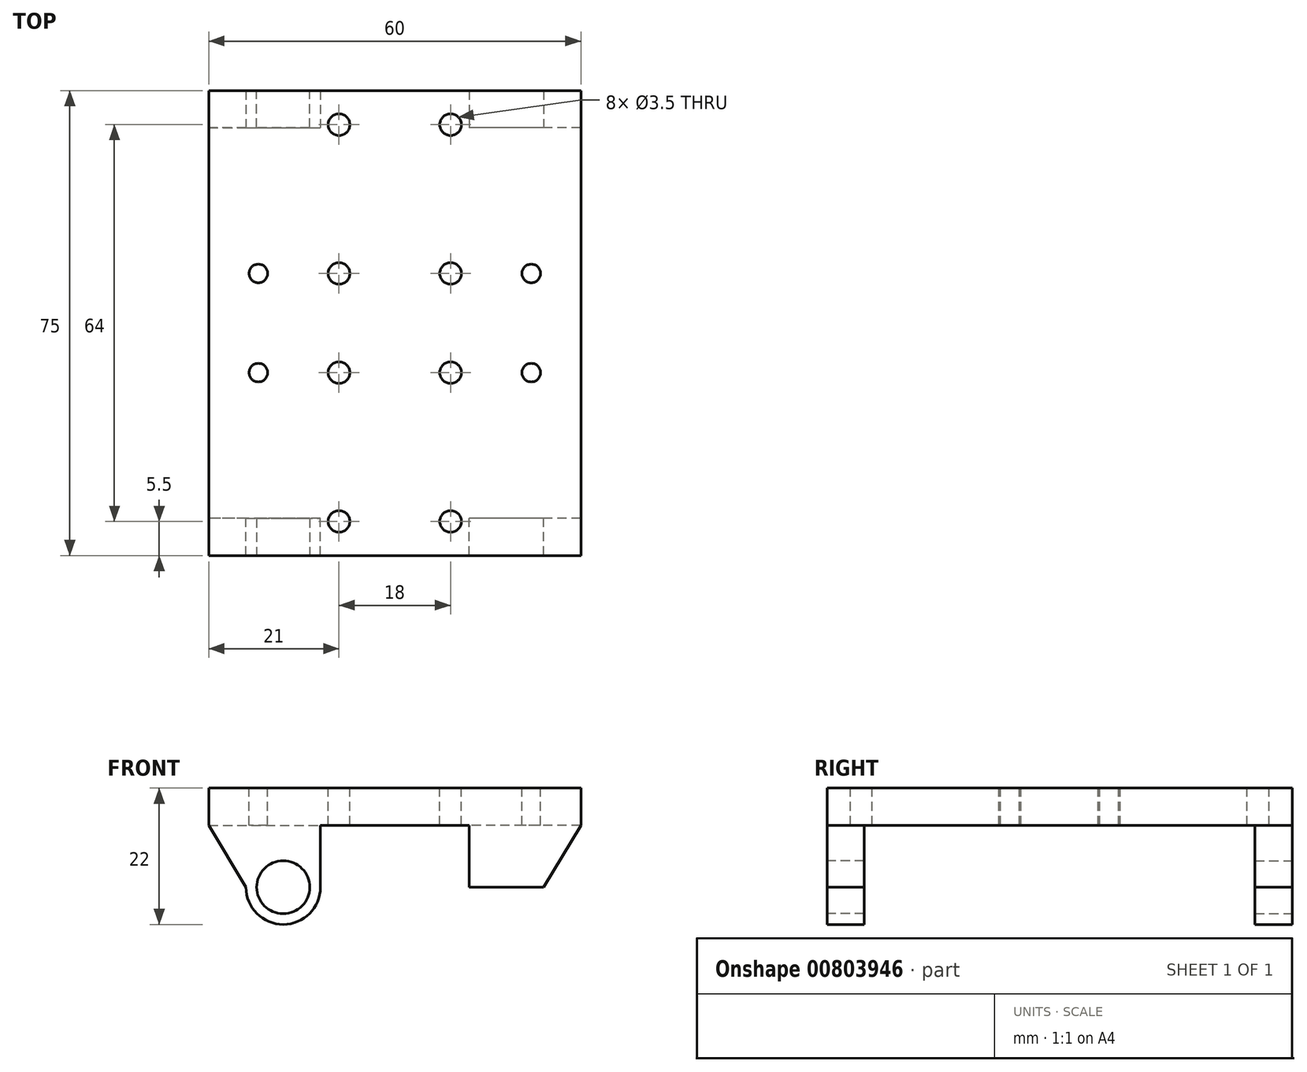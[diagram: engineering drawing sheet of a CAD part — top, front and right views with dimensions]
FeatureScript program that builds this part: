
annotation { "Feature Type Name" : "Feature", "Feature Type Description" : "" }
export const myFeature = defineFeature(function(context is Context, id is Id, definition is map)
    precondition{}
    {
        {
            var Q0;
            Q0=qCreatedBy(makeId("Top.planeOp"),FACE);
            var sketch = newSketch(context, id + "F0", { "sketchPlane" : qUnion([Q0])});
            skLineSegment(sketch, "E0.bottom", {"start": v(30, 37.5) * mm, "end": v(-30, 37.5) * mm});
            skLineSegment(sketch, "E0.top", {"start": v(30, -37.5) * mm, "end": v(-30, -37.5) * mm});
            skLineSegment(sketch, "E0.left", {"start": v(30, 37.5) * mm, "end": v(30, -37.5) * mm});
            skLineSegment(sketch, "E0.right", {"start": v(-30, 37.5) * mm, "end": v(-30, -37.5) * mm});
            skPoint(sketch, "E0.middle", {"position": v(0, 0) * mm});
            skLineSegment(sketch, "E1.bottom", {"start": v(-9, 32) * mm, "end": v(9, 32) * mm});
            skLineSegment(sketch, "E1.top", {"start": v(-9, 8) * mm, "end": v(9, 8) * mm});
            skLineSegment(sketch, "E1.left", {"start": v(-9, 32) * mm, "end": v(-9, 8) * mm});
            skLineSegment(sketch, "E1.right", {"start": v(9, 32) * mm, "end": v(9, 8) * mm});
            skPoint(sketch, "E1.middle", {"position": v(0, 20) * mm});
            skLineSegment(sketch, "E2.bottom", {"start": v(-9, -8) * mm, "end": v(9, -8) * mm});
            skLineSegment(sketch, "E2.top", {"start": v(-9, -32) * mm, "end": v(9, -32) * mm});
            skLineSegment(sketch, "E2.left", {"start": v(-9, -8) * mm, "end": v(-9, -32) * mm});
            skLineSegment(sketch, "E2.right", {"start": v(9, -8) * mm, "end": v(9, -32) * mm});
            skPoint(sketch, "E2.middle", {"position": v(0, -20) * mm});
            skLineSegment(sketch, "E3.bottom", {"start": v(24, 37.5) * mm, "end": v(12, 37.5) * mm});
            skLineSegment(sketch, "E3.top", {"start": v(24, 31.5) * mm, "end": v(12, 31.5) * mm});
            skLineSegment(sketch, "E3.left", {"start": v(24, 37.5) * mm, "end": v(24, 31.5) * mm});
            skLineSegment(sketch, "E3.right", {"start": v(12, 37.5) * mm, "end": v(12, 31.5) * mm});
            skLineSegment(sketch, "E4.bottom", {"start": v(-24, 37.5) * mm, "end": v(-12, 37.5) * mm});
            skLineSegment(sketch, "E4.top", {"start": v(-24, 31.5) * mm, "end": v(-12, 31.5) * mm});
            skLineSegment(sketch, "E4.left", {"start": v(-24, 37.5) * mm, "end": v(-24, 31.5) * mm});
            skLineSegment(sketch, "E4.right", {"start": v(-12, 37.5) * mm, "end": v(-12, 31.5) * mm});
            skLineSegment(sketch, "E5.bottom", {"start": v(24, -37.5) * mm, "end": v(12, -37.5) * mm});
            skLineSegment(sketch, "E5.top", {"start": v(24, -31.5) * mm, "end": v(12, -31.5) * mm});
            skLineSegment(sketch, "E5.left", {"start": v(24, -37.5) * mm, "end": v(24, -31.5) * mm});
            skLineSegment(sketch, "E5.right", {"start": v(12, -37.5) * mm, "end": v(12, -31.5) * mm});
            skLineSegment(sketch, "E6.bottom", {"start": v(-12, -37.5) * mm, "end": v(-24, -37.5) * mm});
            skLineSegment(sketch, "E6.top", {"start": v(-12, -31.5) * mm, "end": v(-24, -31.5) * mm});
            skLineSegment(sketch, "E6.left", {"start": v(-12, -37.5) * mm, "end": v(-12, -31.5) * mm});
            skLineSegment(sketch, "E6.right", {"start": v(-24, -37.5) * mm, "end": v(-24, -31.5) * mm});
            skPoint(sketch, "E7", {"position": v(22, 8) * mm});
            skPoint(sketch, "E8", {"position": v(22, -8) * mm});
            skPoint(sketch, "E9", {"position": v(-22, 8) * mm});
            skPoint(sketch, "E10", {"position": v(-22, -8) * mm});
            skSolve(sketch);
        }
        {
            var Q0;
            {var subQ5=sQuery(id+"F0.wireOp",EDGE,"E0.left");Q0=makeQuery(id+"F0.imprint","IMPRINT",FACE,{"disambiguationData":[TD([[makeQuery(id+"F0.imprint","IMPRINT",EDGE,{"derivedFrom":subQ5}),-1.0]])]});}
            var Q1;
            Q1=makeQuery(id+"F0.imprint","IMPRINT",FACE,{"disambiguationData":[TD([[makeQuery(id+"F0.imprint","IMPRINT",EDGE,{"derivedFrom":sQuery(id+"F0.wireOp",EDGE,"E1.bottom")}),-1.0]])]});
            var Q2;
            Q2=makeQuery(id+"F0.imprint","IMPRINT",FACE,{"disambiguationData":[TD([[makeQuery(id+"F0.imprint","IMPRINT",EDGE,{"derivedFrom":sQuery(id+"F0.wireOp",EDGE,"E2.bottom")}),-1.0]])]});
            var Q3;
            Q3=makeQuery(id+"F0.imprint","IMPRINT",FACE,{"disambiguationData":[TD([[makeQuery(id+"F0.imprint","IMPRINT",EDGE,{"derivedFrom":sQuery(id+"F0.wireOp",EDGE,"E5.top")}),1.0]])]});
            var Q4;
            Q4=makeQuery(id+"F0.imprint","IMPRINT",FACE,{"disambiguationData":[TD([[makeQuery(id+"F0.imprint","IMPRINT",EDGE,{"derivedFrom":sQuery(id+"F0.wireOp",EDGE,"E2.bottom")}),-1.0]])]});
            var Q5;
            {var subQ5=sQuery(id+"F0.wireOp",EDGE,"E0.left");Q5=makeQuery(id+"F0.imprint","IMPRINT",FACE,{"disambiguationData":[TD([[makeQuery(id+"F0.imprint","IMPRINT",EDGE,{"derivedFrom":subQ5}),-1.0]])]});}
            var Q6;
            Q6=makeQuery(id+"F0.imprint","IMPRINT",FACE,{"disambiguationData":[TD([[makeQuery(id+"F0.imprint","IMPRINT",EDGE,{"derivedFrom":sQuery(id+"F0.wireOp",EDGE,"E2.bottom")}),-1.0]])]});
            var Q7;
            Q7=makeQuery(id+"F0.imprint","IMPRINT",FACE,{"disambiguationData":[TD([[makeQuery(id+"F0.imprint","IMPRINT",EDGE,{"derivedFrom":sQuery(id+"F0.wireOp",EDGE,"E6.top")}),1.0]])]});
            var Q8;
            Q8=makeQuery(id+"F0.imprint","IMPRINT",FACE,{"disambiguationData":[TD([[makeQuery(id+"F0.imprint","IMPRINT",EDGE,{"derivedFrom":sQuery(id+"F0.wireOp",EDGE,"E1.bottom")}),-1.0]])]});
            var Q9;
            {var subQ5=sQuery(id+"F0.wireOp",EDGE,"E0.left");Q9=makeQuery(id+"F0.imprint","IMPRINT",FACE,{"disambiguationData":[TD([[makeQuery(id+"F0.imprint","IMPRINT",EDGE,{"derivedFrom":subQ5}),-1.0]])]});}
            var Q10;
            Q10=makeQuery(id+"F0.imprint","IMPRINT",FACE,{"disambiguationData":[TD([[makeQuery(id+"F0.imprint","IMPRINT",EDGE,{"derivedFrom":sQuery(id+"F0.wireOp",EDGE,"E4.top")}),1.0]])]});
            var Q11;
            Q11=makeQuery(id+"F0.imprint","IMPRINT",FACE,{"disambiguationData":[TD([[makeQuery(id+"F0.imprint","IMPRINT",EDGE,{"derivedFrom":sQuery(id+"F0.wireOp",EDGE,"E3.top")}),-1.0]])]});
            extrude(context, id + "F1", {"entities" : qUnion([Q0, Q1, Q2, Q3, Q4, Q5, Q6, Q7, Q8, Q9, Q10, Q11]), "depth" : 6 * mm, "offsetDistance" : 25 * mm});
        }
        {
            var Q0;
            Q0=sQuery(id+"F0.wireOp",VERTEX,"E1.bottom.end");
            var Q1;
            Q1=sQuery(id+"F0.wireOp",VERTEX,"E1.bottom.start");
            var Q2;
            Q2=sQuery(id+"F0.wireOp",VERTEX,"E1.top.start");
            var Q3;
            Q3=sQuery(id+"F0.wireOp",VERTEX,"E1.top.end");
            var Q4;
            Q4=sQuery(id+"F0.wireOp",VERTEX,"E2.bottom.end");
            var Q5;
            Q5=sQuery(id+"F0.wireOp",VERTEX,"E2.bottom.start");
            var Q6;
            Q6=sQuery(id+"F0.wireOp",VERTEX,"E2.top.start");
            var Q7;
            Q7=sQuery(id+"F0.wireOp",VERTEX,"E2.top.end");
            var Q8;
            Q8=makeQuery(id+"F1.opExtrude","SWEPT_BODY",BODY,{"disambiguationData":[OSD([sQuery(id+"F0.wireOp",EDGE,"E0.bottom"),sQuery(id+"F0.wireOp",EDGE,"E0.top"),sQuery(id+"F0.wireOp",EDGE,"E0.left"),sQuery(id+"F0.wireOp",EDGE,"E0.right")])]});
            hole(context, id + "F2", {"style" : HoleStyle.SIMPLE, "endStyle" : HoleEndStyle.THROUGH, "oppositeDirection" : true, "holeDiameter" : 3.5 * mm, "majorDiameter" : 5 * mm, "isTappedThrough" : true, "tappedDepth" : 12 * mm, "tapClearance" : 3, "locations" : qUnion([Q0, Q1, Q2, Q3, Q4, Q5, Q6, Q7]), "scope" : qUnion([Q8])});
        }
        {
            var Q0;
            Q0=makeQuery(id+"F0.imprint","IMPRINT",FACE,{"disambiguationData":[TD([[makeQuery(id+"F0.imprint","IMPRINT",EDGE,{"derivedFrom":sQuery(id+"F0.wireOp",EDGE,"E3.top")}),-1.0]])]});
            var Q1;
            Q1=makeQuery(id+"F0.imprint","IMPRINT",FACE,{"disambiguationData":[TD([[makeQuery(id+"F0.imprint","IMPRINT",EDGE,{"derivedFrom":sQuery(id+"F0.wireOp",EDGE,"E4.top")}),1.0]])]});
            var Q2;
            Q2=makeQuery(id+"F0.imprint","IMPRINT",FACE,{"disambiguationData":[TD([[makeQuery(id+"F0.imprint","IMPRINT",EDGE,{"derivedFrom":sQuery(id+"F0.wireOp",EDGE,"E6.top")}),1.0]])]});
            var Q3;
            Q3=makeQuery(id+"F0.imprint","IMPRINT",FACE,{"disambiguationData":[TD([[makeQuery(id+"F0.imprint","IMPRINT",EDGE,{"derivedFrom":sQuery(id+"F0.wireOp",EDGE,"E5.top")}),1.0]])]});
            extrude(context, id + "F3", {"entities" : qUnion([Q0, Q1, Q2, Q3]), "operationType" : NewBodyOperationType.ADD, "oppositeDirection" : true, "depth" : 10 * mm, "offsetDistance" : 25 * mm});
        }
        {
            var Q0;
            {var subQ0=sQuery(id+"F0.wireOp",EDGE,"E0.top");Q0=makeQuery(id+"F3.boolean.opBoolean","MERGE",FACE,{"derivedFrom":[makeQuery(id+"F1.opExtrude","SWEPT_FACE",FACE,{"disambiguationData":[OSD([subQ0])]}),makeQuery(id+"F3.opExtrude","SWEPT_FACE",FACE,{"disambiguationData":[OSD([subQ0]),TDD([makeQuery(id+"F0.imprint","IMPRINT",EDGE,{"disambiguationData":[TD([[makeQuery(id+"F0.imprint","INTERSECT",VERTEX,{"derivedFrom":[subQ0,sQuery(id+"F0.wireOp",EDGE,"E5.right")]}),1.0]])],"derivedFrom":subQ0})])]}),makeQuery(id+"F3.opExtrude","SWEPT_FACE",FACE,{"disambiguationData":[OSD([subQ0]),TDD([makeQuery(id+"F0.imprint","IMPRINT",EDGE,{"disambiguationData":[TD([[makeQuery(id+"F0.imprint","INTERSECT",VERTEX,{"derivedFrom":[subQ0,sQuery(id+"F0.wireOp",EDGE,"E6.left")]}),-1.0]])],"derivedFrom":subQ0})])]})]});}
            var sketch = newSketch(context, id + "F4", { "sketchPlane" : qUnion([Q0])});
            skLineSegment(sketch, "E11", {"start": v(30, 0) * mm, "end": v(24, -10) * mm});
            skArc(sketch, "E12", {"start": v(24, -10) * mm, "mid": v(18, -16) * mm, "end": v(12, -10) * mm});
            skLineSegment(sketch, "E13", {"start": v(-24, -10) * mm, "end": v(-30, 0) * mm});
            skArc(sketch, "E14", {"start": v(-24, -10) * mm, "mid": v(-18, -16) * mm, "end": v(-12, -10) * mm});
            skCircle(sketch, "E15", {"center": v(18, -10) * mm, "radius": 4.28 * mm});
            skCircle(sketch, "E16", {"center": v(-18, -10) * mm, "radius": 4.28 * mm});
            skSolve(sketch);
        }
        {
            var Q0;
            {var subQ0=sQuery(id+"F4.wireOp",EDGE,"E12");Q0=makeQuery(id+"F4.imprint","IMPRINT",FACE,{"disambiguationData":[TD([[makeQuery(id+"F4.imprint","IMPRINT",EDGE,{"derivedFrom":subQ0}),-1.0]])]});}
            var Q1;
            Q1=makeQuery(id+"F4.imprint","IMPRINT",FACE,{"disambiguationData":[TD([[makeQuery(id+"F4.imprint","IMPRINT",EDGE,{"derivedFrom":sQuery(id+"F4.wireOp",EDGE,"E11")}),-1.0]])]});
            var Q2;
            {var subQ0=sQuery(id+"F4.wireOp",EDGE,"E14");Q2=makeQuery(id+"F4.imprint","IMPRINT",FACE,{"disambiguationData":[TD([[makeQuery(id+"F4.imprint","IMPRINT",EDGE,{"derivedFrom":subQ0}),1.0]])]});}
            var Q3;
            Q3=makeQuery(id+"F4.imprint","IMPRINT",FACE,{"disambiguationData":[TD([[makeQuery(id+"F4.imprint","IMPRINT",EDGE,{"derivedFrom":sQuery(id+"F4.wireOp",EDGE,"E13")}),-1.0]])]});
            extrude(context, id + "F5", {"entities" : qUnion([Q0, Q1, Q2, Q3]), "operationType" : NewBodyOperationType.ADD, "oppositeDirection" : true, "depth" : 6 * mm, "offsetDistance" : 25 * mm});
        }
        {
            var Q0;
            {var subQ0=sQuery(id+"F4.wireOp",EDGE,"E15");var subQ1=sQuery(id+"F0.wireOp",EDGE,"E0.top");var subQ2=makeQuery(id+"F3.opExtrude","CAP_EDGE",EDGE,{"disambiguationData":[OSD([subQ1]),TDD([makeQuery(id+"F0.imprint","IMPRINT",EDGE,{"disambiguationData":[TD([[makeQuery(id+"F0.imprint","INTERSECT",VERTEX,{"derivedFrom":[subQ1,sQuery(id+"F0.wireOp",EDGE,"E5.right")]}),1.0]])],"derivedFrom":subQ1})])],"isStart":false});var subQ3=makeQuery(id+"F4.imprint","INTERSECT",VERTEX,{"disambiguationData":[OD(0.0)],"derivedFrom":[subQ2,subQ0]});Q0=makeQuery(id+"F4.imprint","IMPRINT",FACE,{"disambiguationData":[TD([[makeQuery(id+"F4.imprint","IMPRINT",EDGE,{"disambiguationData":[TD([[subQ3,1.0]])],"derivedFrom":subQ0}),1.0]])]});}
            var Q1;
            {var subQ0=sQuery(id+"F4.wireOp",EDGE,"E16");var subQ1=sQuery(id+"F0.wireOp",EDGE,"E0.top");var subQ2=makeQuery(id+"F3.opExtrude","CAP_EDGE",EDGE,{"disambiguationData":[OSD([subQ1]),TDD([makeQuery(id+"F0.imprint","IMPRINT",EDGE,{"disambiguationData":[TD([[makeQuery(id+"F0.imprint","INTERSECT",VERTEX,{"derivedFrom":[subQ1,sQuery(id+"F0.wireOp",EDGE,"E6.left")]}),-1.0]])],"derivedFrom":subQ1})])],"isStart":false});var subQ3=makeQuery(id+"F4.imprint","INTERSECT",VERTEX,{"disambiguationData":[OD(0.0)],"derivedFrom":[subQ2,subQ0]});Q1=makeQuery(id+"F4.imprint","IMPRINT",FACE,{"disambiguationData":[TD([[makeQuery(id+"F4.imprint","IMPRINT",EDGE,{"disambiguationData":[TD([[subQ3,-1.0]])],"derivedFrom":subQ0}),1.0]])]});}
            extrude(context, id + "F6", {"entities" : qUnion([Q0, Q1]), "operationType" : NewBodyOperationType.REMOVE, "oppositeDirection" : true, "depth" : 25 * mm, "offsetDistance" : 25 * mm});
        }
        {
            var Q0;
            Q0=makeQuery(id+"F1.opExtrude","SWEPT_BODY",BODY,{"disambiguationData":[OSD([sQuery(id+"F0.wireOp",EDGE,"E0.bottom"),sQuery(id+"F0.wireOp",EDGE,"E0.top"),sQuery(id+"F0.wireOp",EDGE,"E0.left"),sQuery(id+"F0.wireOp",EDGE,"E0.right")])]});
            var Q1;
            Q1=qCreatedBy(makeId("Front.planeOp"),FACE);
            mirror(context, id + "F7", {"operationType" : NewBodyOperationType.ADD, "entities" : qUnion([Q0]), "mirrorPlane" : qUnion([Q1])});
        }
        {
            var Q0;
            {var subQ0=sQuery(id+"F4.wireOp",EDGE,"E15");var subQ1=sQuery(id+"F0.wireOp",EDGE,"E0.top");var subQ2=makeQuery(id+"F3.opExtrude","CAP_EDGE",EDGE,{"disambiguationData":[OSD([subQ1]),TDD([makeQuery(id+"F0.imprint","IMPRINT",EDGE,{"disambiguationData":[TD([[makeQuery(id+"F0.imprint","INTERSECT",VERTEX,{"derivedFrom":[subQ1,sQuery(id+"F0.wireOp",EDGE,"E5.right")]}),1.0]])],"derivedFrom":subQ1})])],"isStart":false});var subQ3=makeQuery(id+"F4.imprint","INTERSECT",VERTEX,{"disambiguationData":[OD(0.0)],"derivedFrom":[subQ2,subQ0]});Q0=makeQuery(id+"F4.imprint","IMPRINT",FACE,{"disambiguationData":[TD([[makeQuery(id+"F4.imprint","IMPRINT",EDGE,{"disambiguationData":[TD([[subQ3,1.0]])],"derivedFrom":subQ0}),1.0]])]});}
            var Q1;
            {var subQ0=sQuery(id+"F4.wireOp",EDGE,"E16");var subQ1=sQuery(id+"F0.wireOp",EDGE,"E0.top");var subQ2=makeQuery(id+"F3.opExtrude","CAP_EDGE",EDGE,{"disambiguationData":[OSD([subQ1]),TDD([makeQuery(id+"F0.imprint","IMPRINT",EDGE,{"disambiguationData":[TD([[makeQuery(id+"F0.imprint","INTERSECT",VERTEX,{"derivedFrom":[subQ1,sQuery(id+"F0.wireOp",EDGE,"E6.left")]}),-1.0]])],"derivedFrom":subQ1})])],"isStart":false});var subQ3=makeQuery(id+"F4.imprint","INTERSECT",VERTEX,{"disambiguationData":[OD(0.0)],"derivedFrom":[subQ2,subQ0]});Q1=makeQuery(id+"F4.imprint","IMPRINT",FACE,{"disambiguationData":[TD([[makeQuery(id+"F4.imprint","IMPRINT",EDGE,{"disambiguationData":[TD([[subQ3,-1.0]])],"derivedFrom":subQ0}),1.0]])]});}
            extrude(context, id + "F8", {"entities" : qUnion([Q0, Q1]), "operationType" : NewBodyOperationType.REMOVE, "oppositeDirection" : true, "depth" : 100 * mm, "offsetDistance" : 25 * mm});
        }
        {
            var Q0;
            Q0=sQuery(id+"F0.wireOp",VERTEX,"E7");
            var Q1;
            Q1=sQuery(id+"F0.wireOp",VERTEX,"E8");
            var Q2;
            Q2=sQuery(id+"F0.wireOp",VERTEX,"E9");
            var Q3;
            Q3=sQuery(id+"F0.wireOp",VERTEX,"E10");
            var Q4;
            Q4=makeQuery(id+"F1.opExtrude","SWEPT_BODY",BODY,{"disambiguationData":[OSD([sQuery(id+"F0.wireOp",EDGE,"E0.bottom"),sQuery(id+"F0.wireOp",EDGE,"E0.top"),sQuery(id+"F0.wireOp",EDGE,"E0.left"),sQuery(id+"F0.wireOp",EDGE,"E0.right")])]});
            hole(context, id + "F9", {"style" : HoleStyle.SIMPLE, "endStyle" : HoleEndStyle.THROUGH, "oppositeDirection" : true, "holeDiameter" : 3 * mm, "majorDiameter" : 5 * mm, "isTappedThrough" : true, "tappedDepth" : 12 * mm, "tapClearance" : 3, "locations" : qUnion([Q0, Q1, Q2, Q3]), "scope" : qUnion([Q4])});
        }
    });
